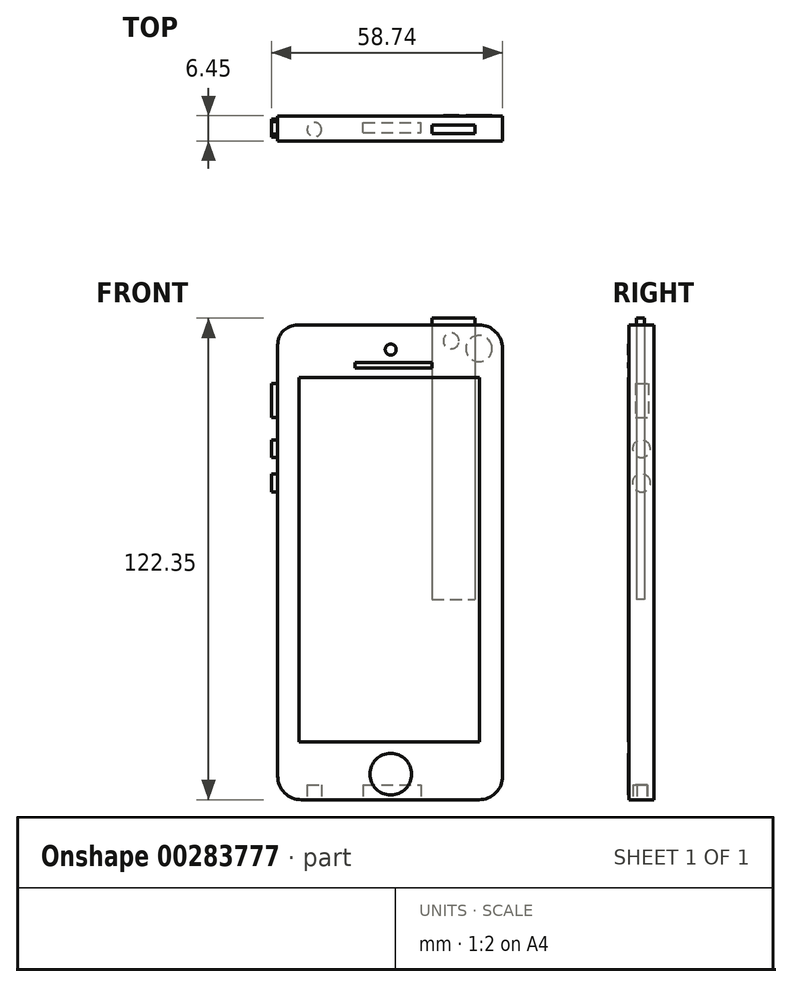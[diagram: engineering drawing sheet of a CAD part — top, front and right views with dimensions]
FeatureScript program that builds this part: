
annotation { "Feature Type Name" : "Feature", "Feature Type Description" : "" }
export const myFeature = defineFeature(function(context is Context, id is Id, definition is map)
    precondition{}
    {
        {
            var Q0;
            Q0=qCreatedBy(makeId("Front.planeOp"),FACE);
            var sketch = newSketch(context, id + "F0", { "sketchPlane" : qUnion([Q0])});
            skLineSegment(sketch, "E0.bottom", {"start": v(-28.71, 69.81) * mm, "end": v(28.44, 69.81) * mm});
            skLineSegment(sketch, "E0.top", {"start": v(-28.71, -50.84) * mm, "end": v(28.44, -50.84) * mm});
            skLineSegment(sketch, "E0.left", {"start": v(-28.71, 69.81) * mm, "end": v(-28.71, -50.84) * mm});
            skLineSegment(sketch, "E0.right", {"start": v(28.44, 69.81) * mm, "end": v(28.44, -50.84) * mm});
            skSolve(sketch);
        }
        {
            var Q0;
            Q0=qSketchRegion(id+"F0",true);
            extrude(context, id + "F1", {"entities" : qUnion([Q0]), "depth" : 6.35 * mm});
        }
        {
            var Q0;
            Q0=makeQuery(id+"F1.opExtrude","SWEPT_EDGE",EDGE,{"disambiguationData":[OSD([sQuery(id+"F0.wireOp",EDGE,"E0.bottom"),sQuery(id+"F0.wireOp",EDGE,"E0.right")])]});
            fillet(context, id + "F2", {"entities" : qUnion([Q0]), "radius" : 6.02 * mm, "tangentPropagation" : true, "allowEdgeOverflow" : false});
        }
        {
            var Q0;
            Q0=makeQuery(id+"F1.opExtrude","SWEPT_EDGE",EDGE,{"disambiguationData":[OSD([sQuery(id+"F0.wireOp",EDGE,"E0.bottom"),sQuery(id+"F0.wireOp",EDGE,"E0.left")])]});
            fillet(context, id + "F3", {"entities" : qUnion([Q0]), "radius" : 5.08 * mm, "tangentPropagation" : true, "allowEdgeOverflow" : false});
        }
        {
            var Q0;
            Q0=makeQuery(id+"F1.opExtrude","SWEPT_EDGE",EDGE,{"disambiguationData":[OSD([sQuery(id+"F0.wireOp",EDGE,"E0.top"),sQuery(id+"F0.wireOp",EDGE,"E0.left")])]});
            fillet(context, id + "F4", {"entities" : qUnion([Q0]), "radius" : 6.02 * mm, "tangentPropagation" : true, "allowEdgeOverflow" : false});
        }
        {
            var Q0;
            Q0=makeQuery(id+"F1.opExtrude","SWEPT_EDGE",EDGE,{"disambiguationData":[OSD([sQuery(id+"F0.wireOp",EDGE,"E0.top"),sQuery(id+"F0.wireOp",EDGE,"E0.right")])]});
            fillet(context, id + "F5", {"entities" : qUnion([Q0]), "radius" : 6.02 * mm, "tangentPropagation" : true, "allowEdgeOverflow" : false});
        }
        {
            var Q0;
            Q0=makeQuery(id+"F1.opExtrude","SWEPT_FACE",FACE,{"disambiguationData":[OSD([sQuery(id+"F0.wireOp",EDGE,"E0.left")])]});
            var sketch = newSketch(context, id + "F6", { "sketchPlane" : qUnion([Q0])});
            skCircle(sketch, "E1", {"center": v(3.14, 38.34) * mm, "radius": 2.24 * mm});
            skCircle(sketch, "E2", {"center": v(3.14, 29.67) * mm, "radius": 2.29 * mm});
            skLineSegment(sketch, "E3.bottom", {"start": v(4.65, 54.96) * mm, "end": v(1.4, 54.96) * mm});
            skLineSegment(sketch, "E3.top", {"start": v(4.65, 46.31) * mm, "end": v(1.4, 46.31) * mm});
            skLineSegment(sketch, "E3.left", {"start": v(4.65, 54.96) * mm, "end": v(4.65, 46.31) * mm});
            skLineSegment(sketch, "E3.right", {"start": v(1.4, 54.96) * mm, "end": v(1.4, 46.31) * mm});
            skLineSegment(sketch, "E4.bottom", {"start": v(4.65, 54.96) * mm, "end": v(3.03, 54.96) * mm});
            skLineSegment(sketch, "E4.top", {"start": v(4.65, 46.31) * mm, "end": v(3.03, 46.31) * mm});
            skLineSegment(sketch, "E4.right", {"start": v(3.03, 54.96) * mm, "end": v(3.03, 46.31) * mm});
            skSolve(sketch);
        }
        {
            var Q0;
            Q0=makeQuery(id+"F6.imprint","IMPRINT",FACE,{"disambiguationData":[TD([[makeQuery(id+"F6.imprint","IMPRINT",EDGE,{"derivedFrom":sQuery(id+"F6.wireOp",EDGE,"E4.bottom")}),1.0]])]});
            var Q1;
            Q1=makeQuery(id+"F6.imprint","IMPRINT",FACE,{"disambiguationData":[TD([[makeQuery(id+"F6.imprint","IMPRINT",EDGE,{"derivedFrom":sQuery(id+"F6.wireOp",EDGE,"E3.bottom")}),1.0]])]});
            var Q2;
            Q2=makeQuery(id+"F6.imprint","IMPRINT",FACE,{"disambiguationData":[TD([[makeQuery(id+"F6.imprint","IMPRINT",EDGE,{"derivedFrom":sQuery(id+"F6.wireOp",EDGE,"E1")}),1.0]])]});
            var Q3;
            Q3=makeQuery(id+"F6.imprint","IMPRINT",FACE,{"disambiguationData":[TD([[makeQuery(id+"F6.imprint","IMPRINT",EDGE,{"derivedFrom":sQuery(id+"F6.wireOp",EDGE,"E2")}),1.0]])]});
            extrude(context, id + "F7", {"entities" : qUnion([Q0, Q1, Q2, Q3]), "depth" : 1.59 * mm});
        }
        {
            var Q0;
            Q0=makeQuery(id+"F1.opExtrude","CAP_FACE",FACE,{"disambiguationData":[OSD([sQuery(id+"F0.wireOp",EDGE,"E0.bottom"),sQuery(id+"F0.wireOp",EDGE,"E0.top"),sQuery(id+"F0.wireOp",EDGE,"E0.left"),sQuery(id+"F0.wireOp",EDGE,"E0.right")])],"isStart":true});
            var sketch = newSketch(context, id + "F8", { "sketchPlane" : qUnion([Q0])});
            skCircle(sketch, "E5", {"center": v(-22.42, 63.8) * mm, "radius": 3.32 * mm});
            skCircle(sketch, "E6", {"center": v(-15.37, 65.74) * mm, "radius": 2 * mm});
            skSolve(sketch);
        }
        {
            var Q0;
            Q0=qCreatedBy(makeId("Top.planeOp"),FACE);
            var sketch = newSketch(context, id + "F9", { "sketchPlane" : qUnion([Q0])});
            skLineSegment(sketch, "E7.bottom", {"start": v(10.47, -2.36) * mm, "end": v(21.37, -2.36) * mm});
            skLineSegment(sketch, "E7.top", {"start": v(10.47, -4.43) * mm, "end": v(21.37, -4.43) * mm});
            skLineSegment(sketch, "E7.left", {"start": v(10.47, -2.36) * mm, "end": v(10.47, -4.43) * mm});
            skLineSegment(sketch, "E7.right", {"start": v(21.37, -2.36) * mm, "end": v(21.37, -4.43) * mm});
            skSolve(sketch);
        }
        {
            var Q0;
            Q0=qSketchRegion(id+"F9",true);
            extrude(context, id + "F10", {"entities" : qUnion([Q0]), "depth" : 71.51 * mm});
        }
        {
            var Q0;
            Q0=makeQuery(id+"F1.opExtrude","CAP_FACE",FACE,{"disambiguationData":[OSD([sQuery(id+"F0.wireOp",EDGE,"E0.bottom"),sQuery(id+"F0.wireOp",EDGE,"E0.top"),sQuery(id+"F0.wireOp",EDGE,"E0.left"),sQuery(id+"F0.wireOp",EDGE,"E0.right")])],"isStart":false});
            var sketch = newSketch(context, id + "F11", { "sketchPlane" : qUnion([Q0])});
            skLineSegment(sketch, "E8.bottom", {"start": v(-23.33, 56.4) * mm, "end": v(22.5, 56.4) * mm});
            skLineSegment(sketch, "E8.top", {"start": v(-23.33, -36.1) * mm, "end": v(22.5, -36.1) * mm});
            skLineSegment(sketch, "E8.left", {"start": v(-23.33, 56.4) * mm, "end": v(-23.33, -36.1) * mm});
            skLineSegment(sketch, "E8.right", {"start": v(22.5, 56.4) * mm, "end": v(22.5, -36.1) * mm});
            skCircle(sketch, "E9", {"center": v(0, -44.33) * mm, "radius": 5.3 * mm});
            skLineSegment(sketch, "E10.bottom", {"start": v(-9.06, 60.25) * mm, "end": v(10.43, 60.25) * mm});
            skLineSegment(sketch, "E10.top", {"start": v(-9.06, 58.88) * mm, "end": v(10.43, 58.88) * mm});
            skLineSegment(sketch, "E10.left", {"start": v(-9.06, 60.25) * mm, "end": v(-9.06, 58.88) * mm});
            skLineSegment(sketch, "E10.right", {"start": v(10.43, 60.25) * mm, "end": v(10.43, 58.88) * mm});
            skCircle(sketch, "E11", {"center": v(0, 63.54) * mm, "radius": 1.4 * mm});
            skSolve(sketch);
        }
        {
            var Q0;
            Q0=qSketchRegion(id+"F11",true);
            extrude(context, id + "F12", {"entities" : qUnion([Q0]), "depth" : 0.05 * mm});
        }
        {
            var Q0;
            Q0=qSketchRegion(id+"F8",true);
            extrude(context, id + "F13", {"entities" : qUnion([Q0]), "depth" : 0.05 * mm});
        }
        {
            var Q0;
            Q0=makeQuery(id+"F1.opExtrude","SWEPT_FACE",FACE,{"disambiguationData":[OSD([sQuery(id+"F0.wireOp",EDGE,"E0.top")])]});
            var sketch = newSketch(context, id + "F14", { "sketchPlane" : qUnion([Q0])});
            skCircle(sketch, "E12", {"center": v(-19.39, 3.49) * mm, "radius": 1.83 * mm});
            skLineSegment(sketch, "E13.bottom", {"start": v(-6.98, 4.28) * mm, "end": v(7.69, 4.28) * mm});
            skLineSegment(sketch, "E13.top", {"start": v(-6.98, 1.71) * mm, "end": v(7.69, 1.71) * mm});
            skLineSegment(sketch, "E13.left", {"start": v(-6.98, 4.28) * mm, "end": v(-6.98, 1.71) * mm});
            skLineSegment(sketch, "E13.right", {"start": v(7.69, 4.28) * mm, "end": v(7.69, 1.71) * mm});
            skSolve(sketch);
        }
        {
            var Q0;
            Q0=qSketchRegion(id+"F14",true);
            extrude(context, id + "F15", {"entities" : qUnion([Q0]), "oppositeDirection" : true, "depth" : 3.82 * mm});
        }
    });
